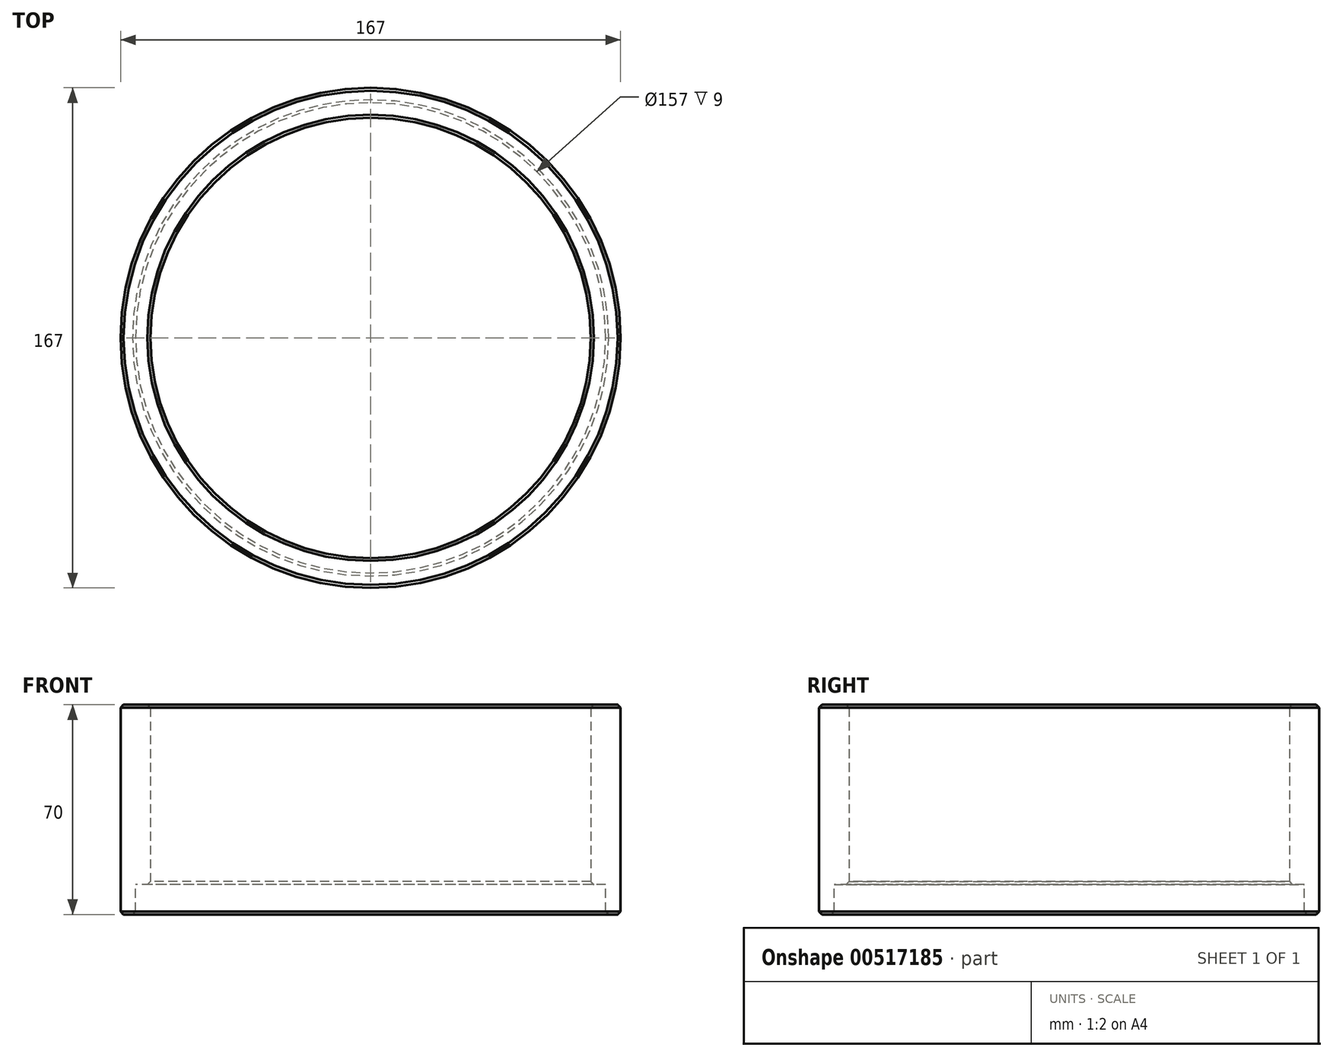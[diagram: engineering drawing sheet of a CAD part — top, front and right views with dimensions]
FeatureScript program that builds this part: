
annotation { "Feature Type Name" : "Feature", "Feature Type Description" : "" }
export const myFeature = defineFeature(function(context is Context, id is Id, definition is map)
    precondition{}
    {
        {
            var Q0;
            Q0=qCreatedBy(makeId("Top.planeOp"),FACE);
            var sketch = newSketch(context, id + "F0", { "sketchPlane" : qUnion([Q0])});
            skCircle(sketch, "E0", {"center": v(0, 0) * mm, "radius": 83.5 * mm});
            skCircle(sketch, "E1", {"center": v(0, 0) * mm, "radius": 78.5 * mm});
            skCircle(sketch, "E2", {"center": v(0, 0) * mm, "radius": 73.5 * mm});
            skSolve(sketch);
        }
        {
            var Q0;
            Q0=makeQuery(id+"F0.imprint","IMPRINT",FACE,{"disambiguationData":[TD([[makeQuery(id+"F0.imprint","IMPRINT",EDGE,{"derivedFrom":sQuery(id+"F0.wireOp",EDGE,"E0")}),1.0]])]});
            var Q1;
            Q1=makeQuery(id+"F0.imprint","IMPRINT",FACE,{"disambiguationData":[TD([[makeQuery(id+"F0.imprint","IMPRINT",EDGE,{"derivedFrom":sQuery(id+"F0.wireOp",EDGE,"E1")}),1.0]])]});
            extrude(context, id + "F1", {"entities" : qUnion([Q0, Q1]), "depth" : 60 * mm, "offsetDistance" : 25 * mm});
        }
        {
            var Q0;
            Q0 = qSketchRegion(id + "F0", true);
            extrude(context, id + "F2", {"entities" : qUnion([Q0]), "operationType" : NewBodyOperationType.ADD, "oppositeDirection" : true, "depth" : 10 * mm, "offsetDistance" : 25 * mm});
        }
        {
            var Q0;
            Q0=makeQuery(id+"F1.opExtrude","CAP_EDGE",EDGE,{"disambiguationData":[OSD([sQuery(id+"F0.wireOp",EDGE,"E2")])],"isStart":false});
            var Q1;
            Q1=makeQuery(id+"F1.opExtrude","CAP_EDGE",EDGE,{"disambiguationData":[OSD([sQuery(id+"F0.wireOp",EDGE,"E0")])],"isStart":false});
            var Q2;
            Q2=makeQuery(id+"F1.opExtrude","CAP_EDGE",EDGE,{"disambiguationData":[OSD([sQuery(id+"F0.wireOp",EDGE,"E2")])],"isStart":true});
            var Q3;
            Q3=makeQuery(id+"F2.opExtrude","CAP_EDGE",EDGE,{"disambiguationData":[OSD([sQuery(id+"F0.wireOp",EDGE,"E1")])],"isStart":false});
            var Q4;
            Q4=makeQuery(id+"F2.opExtrude","CAP_EDGE",EDGE,{"disambiguationData":[OSD([sQuery(id+"F0.wireOp",EDGE,"E0")])],"isStart":false});
            chamfer(context, id + "F3", {"entities" : qUnion([Q0, Q1, Q2, Q3, Q4]), "width" : 1 * mm, "tangentPropagation" : true});
        }
    });
